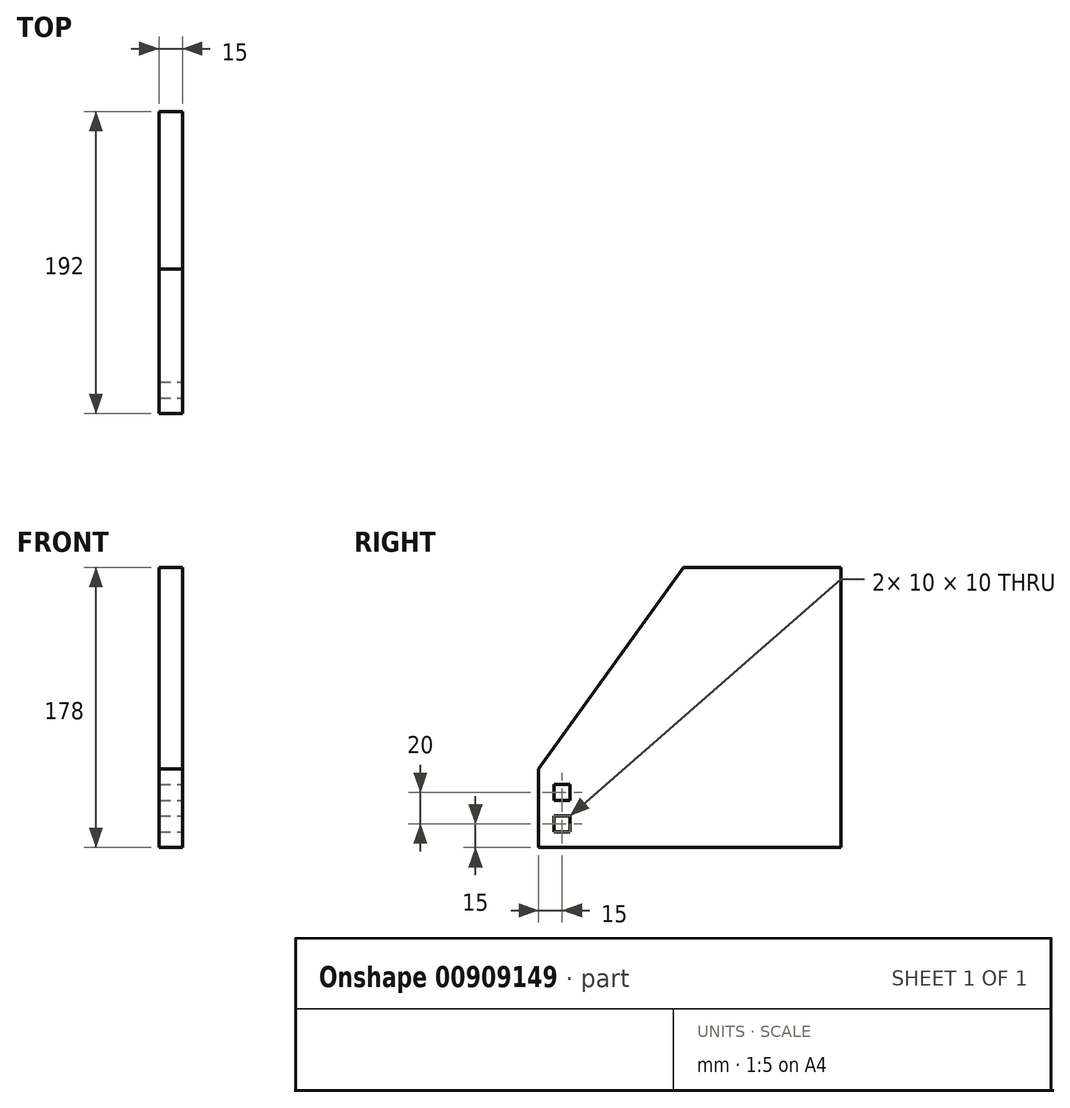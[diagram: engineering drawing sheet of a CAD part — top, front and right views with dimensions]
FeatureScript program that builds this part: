
annotation { "Feature Type Name" : "Feature", "Feature Type Description" : "" }
export const myFeature = defineFeature(function(context is Context, id is Id, definition is map)
    precondition{}
    {
        {
            var Q0;
            Q0=qCreatedBy(makeId("Right.planeOp"),FACE);
            var sketch = newSketch(context, id + "F0", { "sketchPlane" : qUnion([Q0])});
            skLineSegment(sketch, "E0.bottom", {"start": v(96, -89) * mm, "end": v(-96, -89) * mm});
            skLineSegment(sketch, "E0.top", {"start": v(96, 89) * mm, "end": v(-96, 89) * mm});
            skLineSegment(sketch, "E0.left", {"start": v(96, -89) * mm, "end": v(96, 89) * mm});
            skLineSegment(sketch, "E0.right", {"start": v(-96, -89) * mm, "end": v(-96, 89) * mm});
            skPoint(sketch, "E0.middle", {"position": v(0, 0) * mm});
            skLineSegment(sketch, "E1", {"start": v(-4, 89) * mm, "end": v(-96, -39) * mm});
            skSolve(sketch);
        }
        {
            var Q0;
            Q0=makeQuery(id+"F0.imprint","IMPRINT",FACE,{"disambiguationData":[TD([[makeQuery(id+"F0.imprint","IMPRINT",EDGE,{"derivedFrom":sQuery(id+"F0.wireOp",EDGE,"E0.bottom")}),-1.0]])]});
            extrude(context, id + "F1", {"entities" : qUnion([Q0]), "depth" : 15 * mm, "offsetDistance" : 25 * mm});
        }
        {
            var Q0;
            Q0=makeQuery(id+"F1.opExtrude","CAP_FACE",FACE,{"disambiguationData":[OSD([sQuery(id+"F0.wireOp",EDGE,"E0.bottom"),sQuery(id+"F0.wireOp",EDGE,"E0.top"),sQuery(id+"F0.wireOp",EDGE,"E0.left"),sQuery(id+"F0.wireOp",EDGE,"E0.right"),sQuery(id+"F0.wireOp",EDGE,"E1")])],"isStart":false});
            var sketch = newSketch(context, id + "F2", { "sketchPlane" : qUnion([Q0])});
            skLineSegment(sketch, "E2.bottom", {"start": v(-86, -49) * mm, "end": v(-76, -49) * mm});
            skLineSegment(sketch, "E2.top", {"start": v(-86, -79) * mm, "end": v(-76, -79) * mm});
            skLineSegment(sketch, "E3", {"start": v(-86, -59) * mm, "end": v(-76, -59) * mm});
            skLineSegment(sketch, "E4", {"start": v(-86, -69) * mm, "end": v(-76, -69) * mm});
            skLineSegment(sketch, "E5", {"start": v(-86, -49) * mm, "end": v(-86, -59) * mm});
            skLineSegment(sketch, "E6", {"start": v(-76, -49) * mm, "end": v(-76, -59) * mm});
            skLineSegment(sketch, "E7", {"start": v(-86, -69) * mm, "end": v(-86, -79) * mm});
            skLineSegment(sketch, "E8", {"start": v(-76, -69) * mm, "end": v(-76, -79) * mm});
            skSolve(sketch);
        }
        {
            var Q0;
            Q0=makeQuery(id+"F2.imprint","IMPRINT",FACE,{"disambiguationData":[TD([[makeQuery(id+"F2.imprint","IMPRINT",EDGE,{"derivedFrom":sQuery(id+"F2.wireOp",EDGE,"E2.bottom")}),-1.0]])]});
            var Q1;
            Q1=makeQuery(id+"F2.imprint","IMPRINT",FACE,{"disambiguationData":[TD([[makeQuery(id+"F2.imprint","IMPRINT",EDGE,{"derivedFrom":sQuery(id+"F2.wireOp",EDGE,"E2.top")}),1.0]])]});
            extrude(context, id + "F3", {"entities" : qUnion([Q0, Q1]), "operationType" : NewBodyOperationType.REMOVE, "oppositeDirection" : true, "depth" : 15 * mm, "offsetDistance" : 25 * mm});
        }
    });
